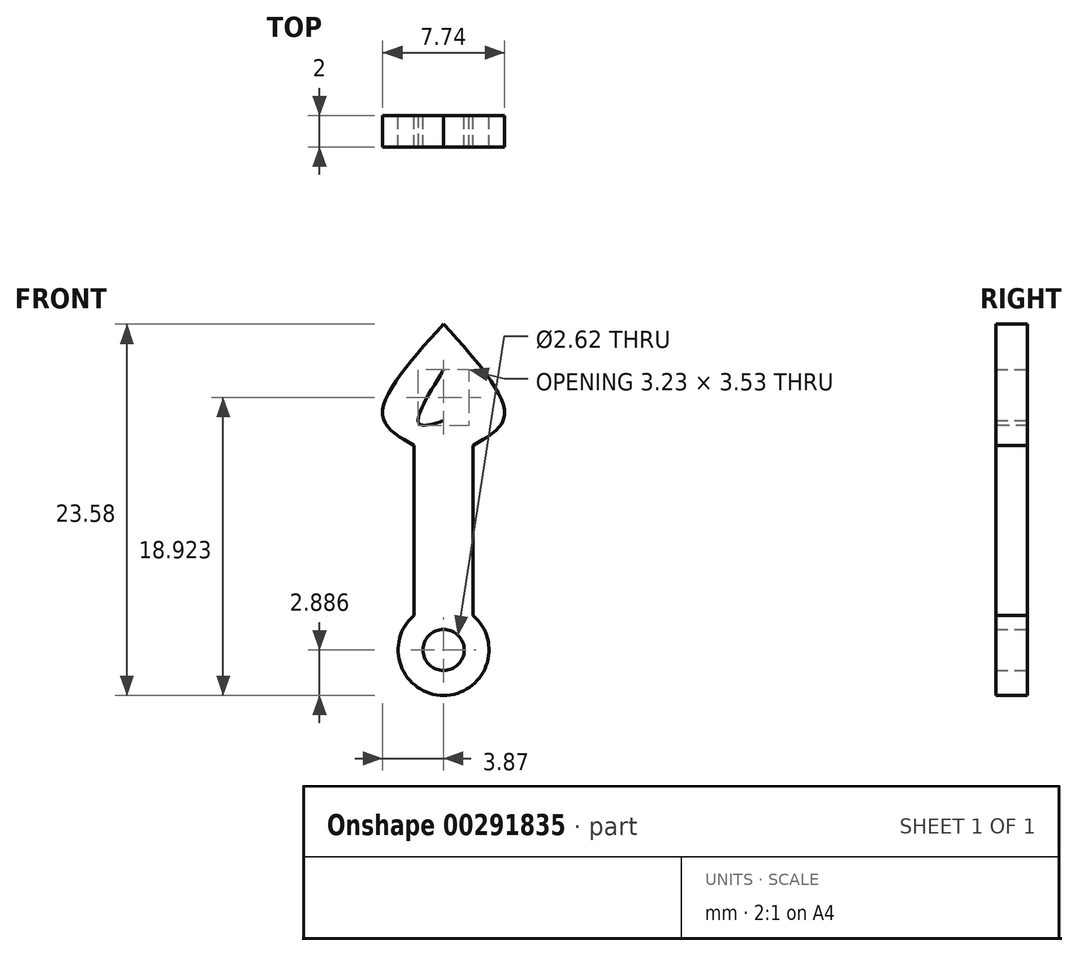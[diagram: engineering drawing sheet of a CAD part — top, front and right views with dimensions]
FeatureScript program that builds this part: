
annotation { "Feature Type Name" : "Feature", "Feature Type Description" : "" }
export const myFeature = defineFeature(function(context is Context, id is Id, definition is map)
    precondition{}
    {
        {
            var Q0;
            Q0=qCreatedBy(makeId("Front.planeOp"),FACE);
            var sketch = newSketch(context, id + "F0", { "sketchPlane" : qUnion([Q0])});
            skFitSpline(sketch, "E0", {"points": [v(0, 26.25) * mm, v(-3.87, 20.46) * mm, v(-1.88, 18.55) * mm], "startDerivative": vector(-9.81, -10.82) * mm, "endDerivative": vector(7.37, -4.06) * mm});
            skFitSpline(sketch, "E1", {"points": [v(0, 23.36) * mm, v(-1.57, 19.94) * mm, v(0, 20.12) * mm], "startDerivative": vector(-4.58, -7.47) * mm, "endDerivative": vector(5.28, 1.64) * mm});
            skFitSpline(sketch, "E2.MirrorCS", {"points": [v(0, 26.25) * mm, v(3.87, 20.46) * mm, v(1.88, 18.55) * mm], "startDerivative": vector(9.81, -10.82) * mm, "endDerivative": vector(-7.37, -4.06) * mm});
            skFitSpline(sketch, "E3.MirrorCS", {"points": [v(0, 23.36) * mm, v(1.57, 19.94) * mm, v(0, 20.12) * mm], "startDerivative": vector(4.58, -7.47) * mm, "endDerivative": vector(-5.28, 1.64) * mm});
            skArc(sketch, "E4", {"start": v(-1.88, 7.75) * mm, "mid": v(0, 2.67) * mm, "end": v(1.88, 7.75) * mm});
            skCircle(sketch, "E5", {"center": v(0, 5.56) * mm, "radius": 1.31 * mm});
            skLineSegment(sketch, "E6.trimOffspring", {"start": v(-1.88, 7.75) * mm, "end": v(-1.88, 18.55) * mm});
            skLineSegment(sketch, "E7.trimOffspring", {"start": v(1.88, 7.75) * mm, "end": v(1.88, 18.55) * mm});
            skPoint(sketch, "E8.end.orphan", {"position": v(0, -3) * mm});
            skSolve(sketch);
        }
        {
            var Q0;
            Q0=makeQuery(id+"F0.imprint","IMPRINT",FACE,{"disambiguationData":[TD([[makeQuery(id+"F0.imprint","IMPRINT",EDGE,{"derivedFrom":sQuery(id+"F0.wireOp",EDGE,"E0")}),1.0]])]});
            extrude(context, id + "F1", {"entities" : qUnion([Q0]), "depth" : 2 * mm});
        }
    });
